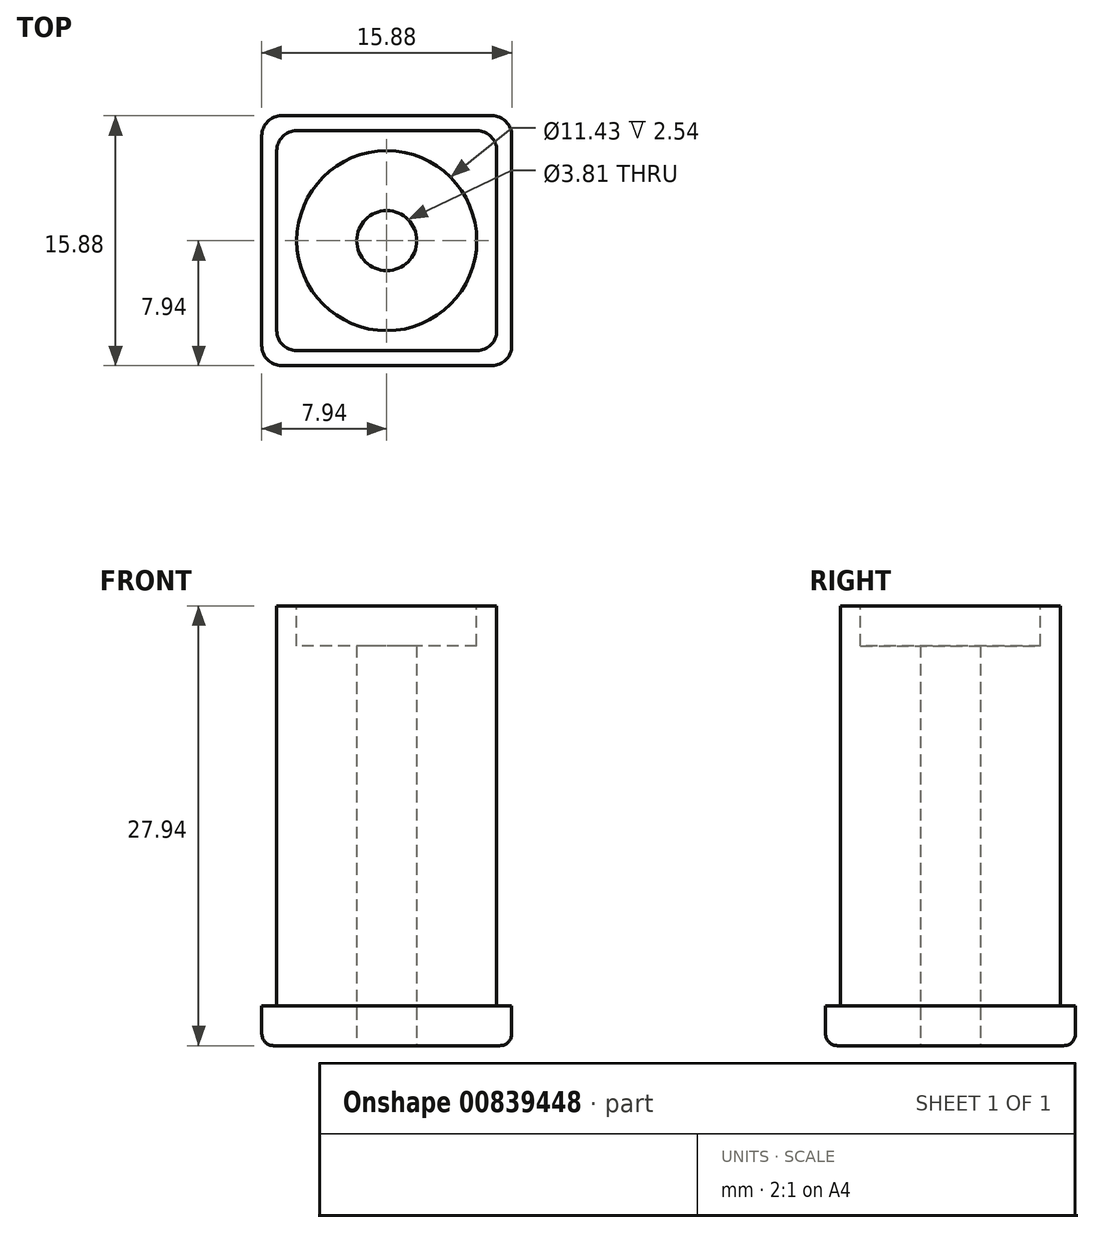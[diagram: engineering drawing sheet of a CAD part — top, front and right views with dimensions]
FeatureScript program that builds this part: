
annotation { "Feature Type Name" : "Feature", "Feature Type Description" : "" }
export const myFeature = defineFeature(function(context is Context, id is Id, definition is map)
    precondition{}
    {
        {
            var Q0;
            Q0=qCreatedBy(makeId("Top.planeOp"),FACE);
            var sketch = newSketch(context, id + "F0", { "sketchPlane" : qUnion([Q0])});
            skLineSegment(sketch, "E0.bottom", {"start": v(6.99, -6.99) * mm, "end": v(-6.99, -6.99) * mm});
            skLineSegment(sketch, "E0.top", {"start": v(6.99, 6.99) * mm, "end": v(-6.99, 6.99) * mm});
            skLineSegment(sketch, "E0.left", {"start": v(6.99, -6.99) * mm, "end": v(6.99, 6.99) * mm});
            skLineSegment(sketch, "E0.right", {"start": v(-6.99, -6.99) * mm, "end": v(-6.99, 6.99) * mm});
            skPoint(sketch, "E0.middle", {"position": v(0, 0) * mm});
            skSolve(sketch);
        }
        {
            var Q0;
            Q0=qSketchRegion(id+"F0",true);
            extrude(context, id + "F1", {"entities" : qUnion([Q0]), "depth" : 25.4 * mm, "offsetDistance" : 25.4 * mm});
        }
        {
            var Q0;
            Q0=makeQuery(id+"F1.opExtrude","CAP_FACE",FACE,{"disambiguationData":[OSD([sQuery(id+"F0.wireOp",EDGE,"E0.bottom"),sQuery(id+"F0.wireOp",EDGE,"E0.top"),sQuery(id+"F0.wireOp",EDGE,"E0.left"),sQuery(id+"F0.wireOp",EDGE,"E0.right")])],"isStart":false});
            var sketch = newSketch(context, id + "F2", { "sketchPlane" : qUnion([Q0])});
            skCircle(sketch, "E1", {"center": v(0, 0) * mm, "radius": 5.72 * mm});
            skSolve(sketch);
        }
        {
            var Q0;
            Q0=qSketchRegion(id+"F2",true);
            extrude(context, id + "F3", {"entities" : qUnion([Q0]), "operationType" : NewBodyOperationType.REMOVE, "oppositeDirection" : true, "depth" : 2.54 * mm, "offsetDistance" : 25.4 * mm});
        }
        {
            var Q0;
            Q0=makeQuery(id+"F1.opExtrude","CAP_FACE",FACE,{"disambiguationData":[OSD([sQuery(id+"F0.wireOp",EDGE,"E0.bottom"),sQuery(id+"F0.wireOp",EDGE,"E0.top"),sQuery(id+"F0.wireOp",EDGE,"E0.left"),sQuery(id+"F0.wireOp",EDGE,"E0.right")])],"isStart":true});
            var sketch = newSketch(context, id + "F4", { "sketchPlane" : qUnion([Q0])});
            skCircle(sketch, "E2", {"center": v(0, 0) * mm, "radius": 1.9 * mm});
            skSolve(sketch);
        }
        {
            var Q0;
            Q0=makeQuery(id+"F1.opExtrude","SWEPT_EDGE",EDGE,{"disambiguationData":[OSD([sQuery(id+"F0.wireOp",EDGE,"E0.top"),sQuery(id+"F0.wireOp",EDGE,"E0.right")])]});
            var Q1;
            Q1=makeQuery(id+"F1.opExtrude","SWEPT_EDGE",EDGE,{"disambiguationData":[OSD([sQuery(id+"F0.wireOp",EDGE,"E0.bottom"),sQuery(id+"F0.wireOp",EDGE,"E0.right")])]});
            var Q2;
            Q2=makeQuery(id+"F1.opExtrude","SWEPT_EDGE",EDGE,{"disambiguationData":[OSD([sQuery(id+"F0.wireOp",EDGE,"E0.top"),sQuery(id+"F0.wireOp",EDGE,"E0.left")])]});
            var Q3;
            Q3=makeQuery(id+"F1.opExtrude","SWEPT_EDGE",EDGE,{"disambiguationData":[OSD([sQuery(id+"F0.wireOp",EDGE,"E0.bottom"),sQuery(id+"F0.wireOp",EDGE,"E0.left")])]});
            fillet(context, id + "F5", {"entities" : qUnion([Q0, Q1, Q2, Q3]), "tangentPropagation" : true, "radius" : 1.27 * mm, "defaultsChanged" : false, "vertexSettings" : [], "allowEdgeOverflow" : false});
        }
        {
            var Q0;
            Q0=makeQuery(id+"F1.opExtrude","CAP_FACE",FACE,{"disambiguationData":[OSD([sQuery(id+"F0.wireOp",EDGE,"E0.bottom"),sQuery(id+"F0.wireOp",EDGE,"E0.top"),sQuery(id+"F0.wireOp",EDGE,"E0.left"),sQuery(id+"F0.wireOp",EDGE,"E0.right")])],"isStart":true});
            var sketch = newSketch(context, id + "F6", { "sketchPlane" : qUnion([Q0])});
            skLineSegment(sketch, "E3.bottom", {"start": v(7.94, -7.94) * mm, "end": v(-7.94, -7.94) * mm});
            skLineSegment(sketch, "E3.top", {"start": v(7.94, 7.94) * mm, "end": v(-7.94, 7.94) * mm});
            skLineSegment(sketch, "E3.left", {"start": v(7.94, -7.94) * mm, "end": v(7.94, 7.94) * mm});
            skLineSegment(sketch, "E3.right", {"start": v(-7.94, -7.94) * mm, "end": v(-7.94, 7.94) * mm});
            skPoint(sketch, "E3.middle", {"position": v(0, 0) * mm});
            skSolve(sketch);
        }
        {
            var Q0;
            Q0 = qSketchRegion(id + "F6", true);
            extrude(context, id + "F7", {"entities" : qUnion([Q0]), "operationType" : NewBodyOperationType.ADD, "depth" : 2.54 * mm, "offsetDistance" : 25.4 * mm});
        }
        {
            var Q0;
            Q0=makeQuery(id+"F7.opExtrude","SWEPT_EDGE",EDGE,{"disambiguationData":[OSD([sQuery(id+"F6.wireOp",EDGE,"E3.top"),sQuery(id+"F6.wireOp",EDGE,"E3.left")])]});
            var Q1;
            Q1=makeQuery(id+"F7.opExtrude","SWEPT_EDGE",EDGE,{"disambiguationData":[OSD([sQuery(id+"F6.wireOp",EDGE,"E3.top"),sQuery(id+"F6.wireOp",EDGE,"E3.right")])]});
            var Q2;
            Q2=makeQuery(id+"F7.opExtrude","SWEPT_EDGE",EDGE,{"disambiguationData":[OSD([sQuery(id+"F6.wireOp",EDGE,"E3.bottom"),sQuery(id+"F6.wireOp",EDGE,"E3.right")])]});
            var Q3;
            Q3=makeQuery(id+"F7.opExtrude","SWEPT_EDGE",EDGE,{"disambiguationData":[OSD([sQuery(id+"F6.wireOp",EDGE,"E3.bottom"),sQuery(id+"F6.wireOp",EDGE,"E3.left")])]});
            fillet(context, id + "F8", {"entities" : qUnion([Q0, Q1, Q2, Q3]), "tangentPropagation" : true, "radius" : 1.27 * mm, "defaultsChanged" : true, "vertexSettings" : [], "allowEdgeOverflow" : false});
        }
        {
            var Q0;
            Q0=makeQuery(id+"F7.opExtrude","CAP_EDGE",EDGE,{"disambiguationData":[OSD([sQuery(id+"F6.wireOp",EDGE,"E3.top")])],"isStart":false});
            fillet(context, id + "F9", {"entities" : qUnion([Q0]), "tangentPropagation" : true, "radius" : 0.76 * mm, "defaultsChanged" : true, "vertexSettings" : [], "allowEdgeOverflow" : false});
        }
        {
            var Q0;
            Q0=qSketchRegion(id+"F4",true);
            extrude(context, id + "F10", {"entities" : qUnion([Q0]), "operationType" : NewBodyOperationType.REMOVE, "endBound" : BoundingType.THROUGH_ALL, "oppositeDirection" : true, "depth" : 12.7 * mm, "offsetDistance" : 25.4 * mm, "hasSecondDirection" : true, "secondDirectionBound" : BoundingType.THROUGH_ALL, "secondDirectionOppositeDirection" : false, "secondDirectionDepth" : 25.4 * mm});
        }
    });
